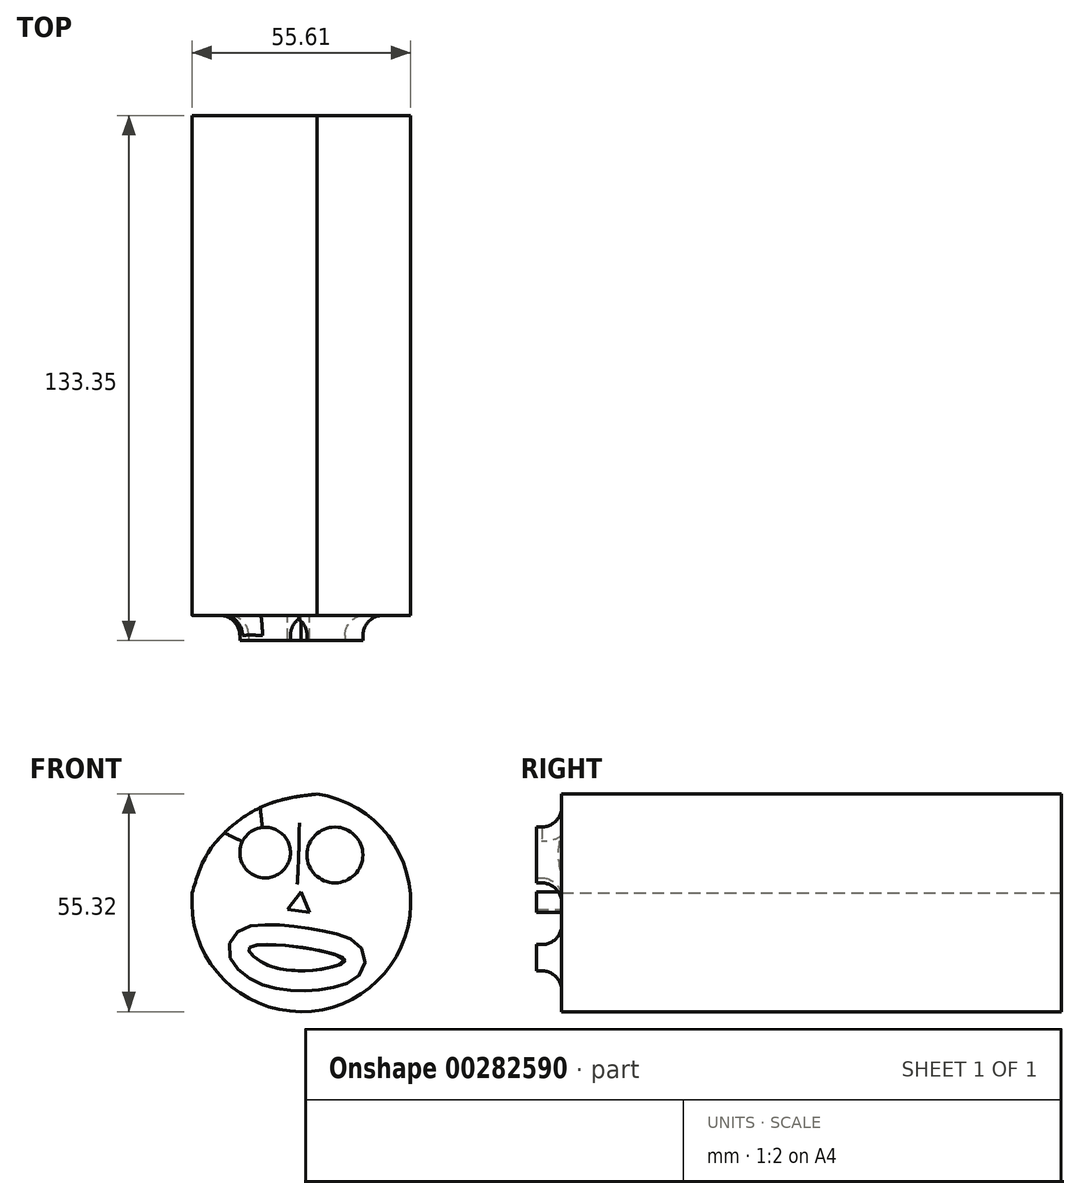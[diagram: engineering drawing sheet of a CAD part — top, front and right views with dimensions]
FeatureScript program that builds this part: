
annotation { "Feature Type Name" : "Feature", "Feature Type Description" : "" }
export const myFeature = defineFeature(function(context is Context, id is Id, definition is map)
    precondition{}
    {
        {
            var Q0;
            Q0=qCreatedBy(makeId("Front.planeOp"),FACE);
            var sketch = newSketch(context, id + "F0", { "sketchPlane" : qUnion([Q0])});
            skArc(sketch, "E0", {"start": v(-31.68, 0) * mm, "mid": v(13.31, -24.13) * mm, "end": v(0, 25.16) * mm});
            skPoint(sketch, "E1.2.internal.snap0", {"position": v(13.31, -24.13) * mm});
            skFitSpline(sketch, "E2", {"points": [v(-31.68, 0) * mm, v(-27.02, 11.18) * mm, v(-13.98, 21.9) * mm, v(0, 25.16) * mm], "startDerivative": vector(10.45, 36.98) * mm, "endDerivative": vector(42.03, 5.15) * mm});
            skSolve(sketch);
        }
        {
            var Q0;
            Q0=makeQuery(id+"F0.imprint","IMPRINT",FACE,{"disambiguationData":[TD([[makeQuery(id+"F0.imprint","IMPRINT",EDGE,{"derivedFrom":sQuery(id+"F0.wireOp",EDGE,"E0")}),1.0]])]});
            extrude(context, id + "F1", {"entities" : qUnion([Q0]), "depth" : 127 * mm});
        }
        {
            var Q0;
            Q0=qCreatedBy(makeId("Front.planeOp"),FACE);
            var sketch = newSketch(context, id + "F2", { "sketchPlane" : qUnion([Q0])});
            skCircle(sketch, "E3", {"center": v(-13.16, 10.26) * mm, "radius": 6.43 * mm});
            skCircle(sketch, "E4", {"center": v(4.58, 9.65) * mm, "radius": 7.1 * mm});
            skFitSpline(sketch, "E5", {"points": [v(-17.07, -13.8) * mm, v(-13.16, -18.02) * mm, v(-7.45, -19.52) * mm, v(0, -19.52) * mm, v(6.99, -16.82) * mm, v(-17.07, -13.8) * mm]});
            skCircle(sketch, "E6.cCircle", {"center": v(-4.44, -2.98) * mm, "radius": 3.23 * mm, "construction": true});
            skLineSegment(sketch, "E6.0", {"start": v(-1.9, -4.98) * mm, "end": v(-7.44, -4.17) * mm});
            skLineSegment(sketch, "E6.1", {"start": v(-7.44, -4.17) * mm, "end": v(-3.97, 0.21) * mm});
            skLineSegment(sketch, "E6.2", {"start": v(-3.97, 0.21) * mm, "end": v(-1.9, -4.98) * mm});
            skSolve(sketch);
        }
        {
            var Q0;
            Q0=makeQuery(id+"F2.imprint","IMPRINT",FACE,{"disambiguationData":[TD([[makeQuery(id+"F2.imprint","IMPRINT",EDGE,{"derivedFrom":sQuery(id+"F2.wireOp",EDGE,"E4")}),1.0]])]});
            var Q1;
            Q1=makeQuery(id+"F2.imprint","IMPRINT",FACE,{"disambiguationData":[TD([[makeQuery(id+"F2.imprint","IMPRINT",EDGE,{"derivedFrom":sQuery(id+"F2.wireOp",EDGE,"E3")}),1.0]])]});
            var Q2;
            Q2=makeQuery(id+"F2.imprint","IMPRINT",FACE,{"disambiguationData":[TD([[makeQuery(id+"F2.imprint","IMPRINT",EDGE,{"derivedFrom":sQuery(id+"F2.wireOp",EDGE,"E5")}),1.0]])]});
            var Q3;
            Q3=makeQuery(id+"F2.imprint","IMPRINT",FACE,{"disambiguationData":[TD([[makeQuery(id+"F2.imprint","IMPRINT",EDGE,{"derivedFrom":sQuery(id+"F2.wireOp",EDGE,"E6.0")}),-1.0]])]});
            extrude(context, id + "F3", {"entities" : qUnion([Q0, Q1, Q2, Q3]), "operationType" : NewBodyOperationType.ADD, "depth" : 133.35 * mm});
        }
        {
            var Q0;
            Q0=makeQuery(id+"F3.boolean.opBoolean","INTERSECT",EDGE,{"derivedFrom":[makeQuery(id+"F1.opExtrude","CAP_FACE",FACE,{"disambiguationData":[OSD([sQuery(id+"F0.wireOp",EDGE,"E0"),sQuery(id+"F0.wireOp",EDGE,"E2")])],"isStart":false}),makeQuery(id+"F3.opExtrude","SWEPT_FACE",FACE,{"disambiguationData":[OSD([sQuery(id+"F2.wireOp",EDGE,"E4")])]})]});
            var Q1;
            Q1=makeQuery(id+"F3.boolean.opBoolean","INTERSECT",EDGE,{"derivedFrom":[makeQuery(id+"F1.opExtrude","CAP_FACE",FACE,{"disambiguationData":[OSD([sQuery(id+"F0.wireOp",EDGE,"E0"),sQuery(id+"F0.wireOp",EDGE,"E2")])],"isStart":false}),makeQuery(id+"F3.opExtrude","SWEPT_FACE",FACE,{"disambiguationData":[OSD([sQuery(id+"F2.wireOp",EDGE,"E3")])]})]});
            var Q2;
            Q2=makeQuery(id+"F3.boolean.opBoolean","INTERSECT",EDGE,{"derivedFrom":[makeQuery(id+"F1.opExtrude","CAP_FACE",FACE,{"disambiguationData":[OSD([sQuery(id+"F0.wireOp",EDGE,"E0"),sQuery(id+"F0.wireOp",EDGE,"E2")])],"isStart":false}),makeQuery(id+"F3.opExtrude","SWEPT_FACE",FACE,{"disambiguationData":[OSD([sQuery(id+"F2.wireOp",EDGE,"E5")])]})]});
            fillet(context, id + "F4", {"entities" : qUnion([Q0, Q1, Q2]), "radius" : 5.08 * mm, "tangentPropagation" : true, "allowEdgeOverflow" : false});
        }
    });
